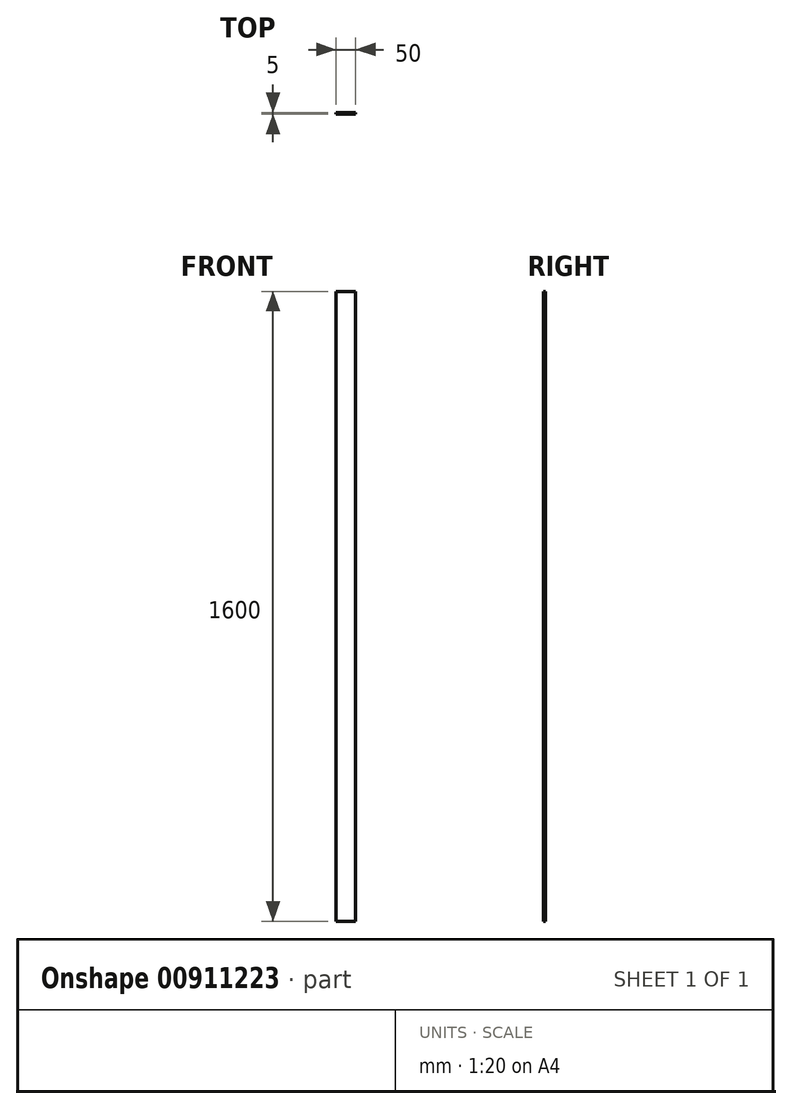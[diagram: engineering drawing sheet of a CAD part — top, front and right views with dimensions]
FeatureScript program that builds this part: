
annotation { "Feature Type Name" : "Feature", "Feature Type Description" : "" }
export const myFeature = defineFeature(function(context is Context, id is Id, definition is map)
    precondition{}
    {
        {
            var Q0;
            Q0=qCreatedBy(makeId("Front.planeOp"),FACE);
            var sketch = newSketch(context, id + "F0", { "sketchPlane" : qUnion([Q0])});
            skLineSegment(sketch, "E0.bottom", {"start": v(25, 800) * mm, "end": v(-25, 800) * mm});
            skLineSegment(sketch, "E0.top", {"start": v(25, -800) * mm, "end": v(-25, -800) * mm});
            skLineSegment(sketch, "E0.left", {"start": v(25, 800) * mm, "end": v(25, -800) * mm});
            skLineSegment(sketch, "E0.right", {"start": v(-25, 800) * mm, "end": v(-25, -800) * mm});
            skPoint(sketch, "E0.middle", {"position": v(0, 0) * mm});
            skSolve(sketch);
        }
        {
            var Q0;
            Q0=makeQuery(id+"F0.imprint","IMPRINT",FACE,{"disambiguationData":[TD([[makeQuery(id+"F0.imprint","IMPRINT",EDGE,{"derivedFrom":sQuery(id+"F0.wireOp",EDGE,"E0.bottom")}),1.0]])]});
            extrude(context, id + "F1", {"entities" : qUnion([Q0]), "depth" : 5 * mm, "offsetDistance" : 25 * mm});
        }
    });
